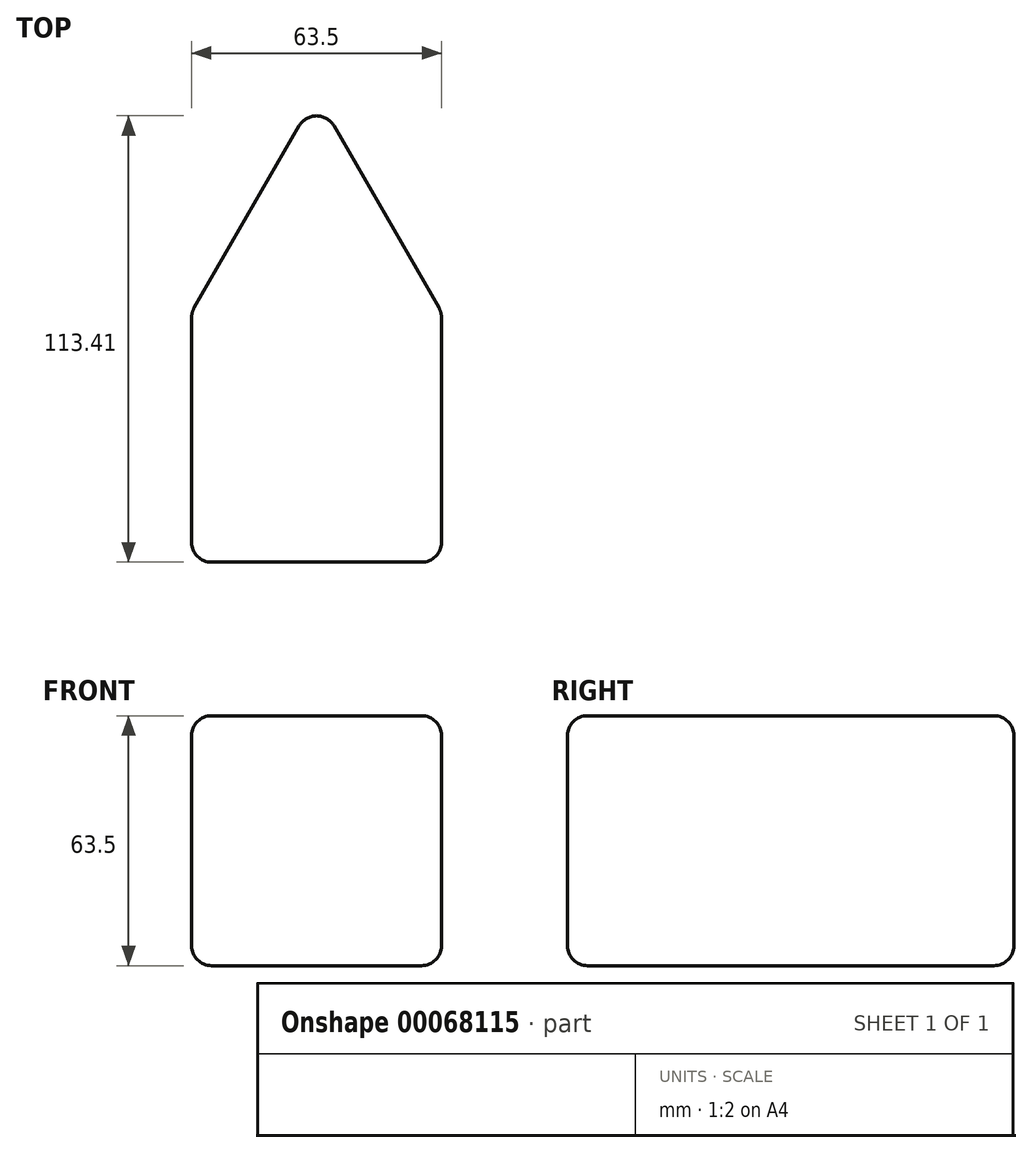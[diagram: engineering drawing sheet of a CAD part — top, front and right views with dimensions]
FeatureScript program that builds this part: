
annotation { "Feature Type Name" : "Feature", "Feature Type Description" : "" }
export const myFeature = defineFeature(function(context is Context, id is Id, definition is map)
    precondition{}
    {
        {
            var Q0;
            Q0=qCreatedBy(makeId("Top.planeOp"),FACE);
            var sketch = newSketch(context, id + "F0", { "sketchPlane" : qUnion([Q0])});
            skLineSegment(sketch, "E0.bottom", {"start": v(0, 0) * mm, "end": v(63.5, 0) * mm});
            skLineSegment(sketch, "E0.left", {"start": v(0, 0) * mm, "end": v(0, 63.5) * mm});
            skLineSegment(sketch, "E0.right", {"start": v(63.5, 0) * mm, "end": v(63.5, 63.5) * mm});
            skLineSegment(sketch, "E1", {"start": v(0, 63.5) * mm, "end": v(31.75, 118.5) * mm});
            skLineSegment(sketch, "E2", {"start": v(31.75, 118.5) * mm, "end": v(63.5, 63.5) * mm});
            skSolve(sketch);
        }
        {
            var Q0;
            Q0=makeQuery(id+"F0.imprint","IMPRINT",FACE,{"disambiguationData":[TD([[makeQuery(id+"F0.imprint","IMPRINT",EDGE,{"derivedFrom":sQuery(id+"F0.wireOp",EDGE,"E0.bottom")}),1.0]])]});
            extrude(context, id + "F1", {"entities" : qUnion([Q0]), "depth" : 63.5 * mm});
        }
        {
            var Q0;
            Q0=makeQuery(id+"F1.opExtrude","CAP_FACE",FACE,{"disambiguationData":[OSD([sQuery(id+"F0.wireOp",EDGE,"E0.bottom"),sQuery(id+"F0.wireOp",EDGE,"E0.left"),sQuery(id+"F0.wireOp",EDGE,"E0.right"),sQuery(id+"F0.wireOp",EDGE,"E1"),sQuery(id+"F0.wireOp",EDGE,"E2")])],"isStart":false});
            var Q1;
            Q1=makeQuery(id+"F1.opExtrude","SWEPT_FACE",FACE,{"disambiguationData":[OSD([sQuery(id+"F0.wireOp",EDGE,"E0.right")])]});
            var Q2;
            Q2=makeQuery(id+"F1.opExtrude","SWEPT_FACE",FACE,{"disambiguationData":[OSD([sQuery(id+"F0.wireOp",EDGE,"E2")])]});
            var Q3;
            Q3=makeQuery(id+"F1.opExtrude","SWEPT_FACE",FACE,{"disambiguationData":[OSD([sQuery(id+"F0.wireOp",EDGE,"E0.bottom")])]});
            var Q4;
            Q4=makeQuery(id+"F1.opExtrude","SWEPT_FACE",FACE,{"disambiguationData":[OSD([sQuery(id+"F0.wireOp",EDGE,"E0.left")])]});
            var Q5;
            Q5=makeQuery(id+"F1.opExtrude","CAP_FACE",FACE,{"disambiguationData":[OSD([sQuery(id+"F0.wireOp",EDGE,"E0.bottom"),sQuery(id+"F0.wireOp",EDGE,"E0.left"),sQuery(id+"F0.wireOp",EDGE,"E0.right"),sQuery(id+"F0.wireOp",EDGE,"E1"),sQuery(id+"F0.wireOp",EDGE,"E2")])],"isStart":true});
            fillet(context, id + "F2", {"entities" : qUnion([Q0, Q1, Q2, Q3, Q4, Q5]), "radius" : 5.08 * mm, "tangentPropagation" : true, "allowEdgeOverflow" : false});
        }
    });
